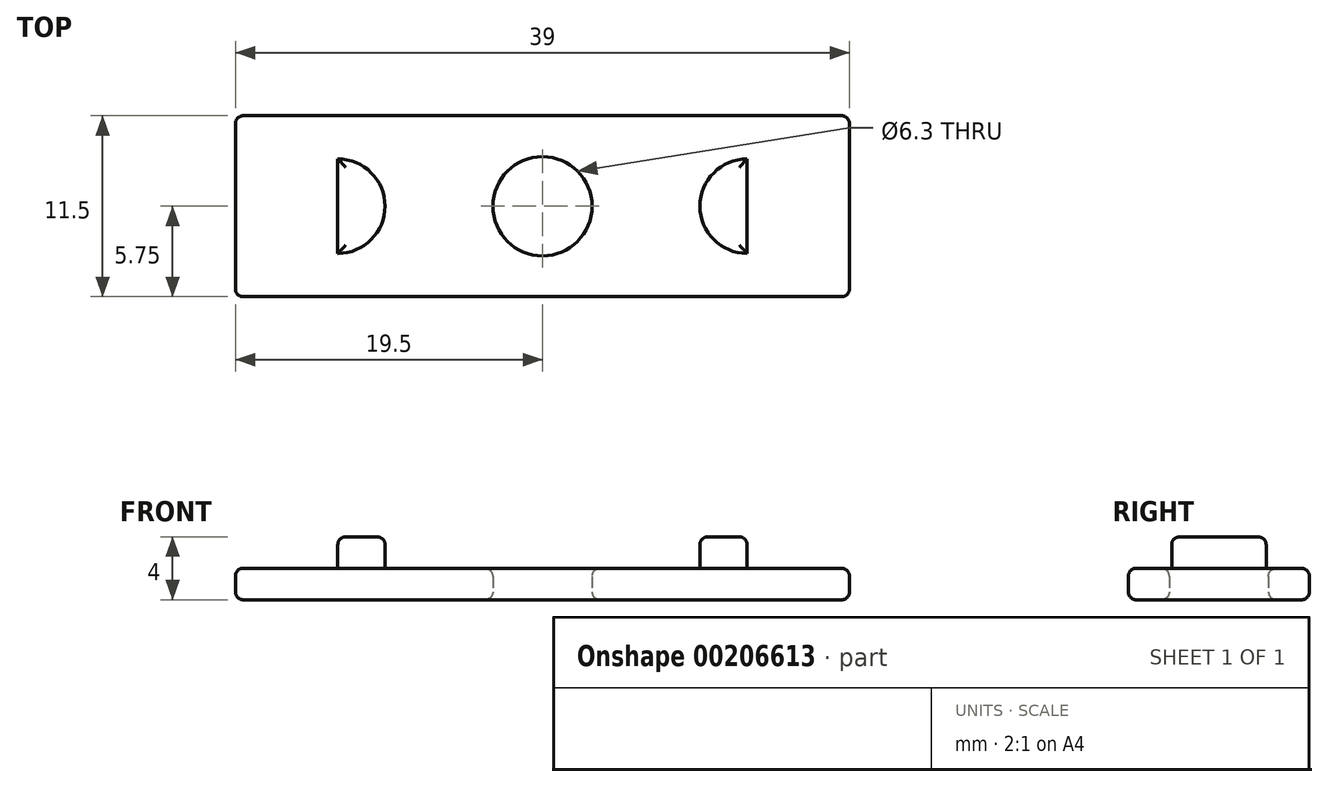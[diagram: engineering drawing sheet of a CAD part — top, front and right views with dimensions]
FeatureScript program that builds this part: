
annotation { "Feature Type Name" : "Feature", "Feature Type Description" : "" }
export const myFeature = defineFeature(function(context is Context, id is Id, definition is map)
    precondition{}
    {
        {
            var Q0;
            Q0=qCreatedBy(makeId("Top.planeOp"),FACE);
            var sketch = newSketch(context, id + "F0", { "sketchPlane" : qUnion([Q0])});
            skLineSegment(sketch, "E0.bottom", {"start": v(-19.5, 5.75) * mm, "end": v(19.5, 5.75) * mm});
            skLineSegment(sketch, "E0.top", {"start": v(-19.5, -5.75) * mm, "end": v(19.5, -5.75) * mm});
            skLineSegment(sketch, "E0.left", {"start": v(-19.5, 5.75) * mm, "end": v(-19.5, -5.75) * mm});
            skLineSegment(sketch, "E0.right", {"start": v(19.5, 5.75) * mm, "end": v(19.5, -5.75) * mm});
            skCircle(sketch, "E1", {"center": v(0, 0) * mm, "radius": 3.15 * mm});
            skSolve(sketch);
        }
        {
            var Q0;
            Q0 = qSketchRegion(id + "F0", true);
            extrude(context, id + "F1", {"entities" : qUnion([Q0]), "depth" : 2 * mm});
        }
        {
            var Q0;
            Q0=makeQuery(id+"F1.opExtrude","CAP_FACE",FACE,{"disambiguationData":[OSD([sQuery(id+"F0.wireOp",EDGE,"E0.bottom"),sQuery(id+"F0.wireOp",EDGE,"E0.top"),sQuery(id+"F0.wireOp",EDGE,"E0.left"),sQuery(id+"F0.wireOp",EDGE,"E0.right"),sQuery(id+"F0.wireOp",EDGE,"E1")])],"isStart":false});
            var sketch = newSketch(context, id + "F2", { "sketchPlane" : qUnion([Q0])});
            skArc(sketch, "E2", {"start": v(-13, -3) * mm, "mid": v(-10, 0) * mm, "end": v(-13, 3) * mm});
            skArc(sketch, "E3.MirrorC", {"start": v(13, -3) * mm, "mid": v(10, 0) * mm, "end": v(13, 3) * mm});
            skLineSegment(sketch, "E4", {"start": v(-13, 3) * mm, "end": v(-13, -3) * mm});
            skLineSegment(sketch, "E5.MirrorCS", {"start": v(13, 3) * mm, "end": v(13, -3) * mm});
            skSolve(sketch);
        }
        {
            var Q0;
            Q0 = qSketchRegion(id + "F2", true);
            extrude(context, id + "F3", {"entities" : qUnion([Q0]), "depth" : 2 * mm});
        }
        {
            var Q0;
            Q0=makeQuery(id+"F1.opExtrude","CAP_EDGE",EDGE,{"disambiguationData":[OSD([sQuery(id+"F0.wireOp",EDGE,"E1")])],"isStart":false});
            var Q1;
            Q1=makeQuery(id+"F1.opExtrude","CAP_EDGE",EDGE,{"disambiguationData":[OSD([sQuery(id+"F0.wireOp",EDGE,"E0.left")])],"isStart":true});
            var Q2;
            Q2=makeQuery(id+"F1.opExtrude","CAP_EDGE",EDGE,{"disambiguationData":[OSD([sQuery(id+"F0.wireOp",EDGE,"E0.right")])],"isStart":true});
            var Q3;
            Q3=makeQuery(id+"F1.opExtrude","CAP_EDGE",EDGE,{"disambiguationData":[OSD([sQuery(id+"F0.wireOp",EDGE,"E0.bottom")])],"isStart":true});
            var Q4;
            Q4=makeQuery(id+"F1.opExtrude","SWEPT_EDGE",EDGE,{"disambiguationData":[OSD([sQuery(id+"F0.wireOp",EDGE,"E0.bottom"),sQuery(id+"F0.wireOp",EDGE,"E0.right")])]});
            var Q5;
            Q5=makeQuery(id+"F1.opExtrude","SWEPT_EDGE",EDGE,{"disambiguationData":[OSD([sQuery(id+"F0.wireOp",EDGE,"E0.top"),sQuery(id+"F0.wireOp",EDGE,"E0.right")])]});
            var Q6;
            Q6=makeQuery(id+"F1.opExtrude","CAP_EDGE",EDGE,{"disambiguationData":[OSD([sQuery(id+"F0.wireOp",EDGE,"E0.bottom")])],"isStart":false});
            var Q7;
            Q7=makeQuery(id+"F1.opExtrude","SWEPT_EDGE",EDGE,{"disambiguationData":[OSD([sQuery(id+"F0.wireOp",EDGE,"E0.bottom"),sQuery(id+"F0.wireOp",EDGE,"E0.left")])]});
            var Q8;
            Q8=makeQuery(id+"F1.opExtrude","CAP_EDGE",EDGE,{"disambiguationData":[OSD([sQuery(id+"F0.wireOp",EDGE,"E0.left")])],"isStart":false});
            var Q9;
            Q9=makeQuery(id+"F1.opExtrude","SWEPT_EDGE",EDGE,{"disambiguationData":[OSD([sQuery(id+"F0.wireOp",EDGE,"E0.top"),sQuery(id+"F0.wireOp",EDGE,"E0.left")])]});
            var Q10;
            Q10=makeQuery(id+"F1.opExtrude","CAP_EDGE",EDGE,{"disambiguationData":[OSD([sQuery(id+"F0.wireOp",EDGE,"E0.top")])],"isStart":false});
            var Q11;
            Q11=makeQuery(id+"F1.opExtrude","CAP_FACE",FACE,{"disambiguationData":[OSD([sQuery(id+"F0.wireOp",EDGE,"E0.bottom"),sQuery(id+"F0.wireOp",EDGE,"E0.top"),sQuery(id+"F0.wireOp",EDGE,"E0.left"),sQuery(id+"F0.wireOp",EDGE,"E0.right"),sQuery(id+"F0.wireOp",EDGE,"E1")])],"isStart":false});
            var Q12;
            Q12=makeQuery(id+"F1.opExtrude","CAP_EDGE",EDGE,{"disambiguationData":[OSD([sQuery(id+"F0.wireOp",EDGE,"E0.top")])],"isStart":true});
            var Q13;
            Q13=makeQuery(id+"F1.opExtrude","CAP_EDGE",EDGE,{"disambiguationData":[OSD([sQuery(id+"F0.wireOp",EDGE,"E1")])],"isStart":true});
            var Q14;
            Q14=makeQuery(id+"F3.opExtrude","CAP_EDGE",EDGE,{"disambiguationData":[OSD([sQuery(id+"F2.wireOp",EDGE,"E3.MirrorC")])],"isStart":false});
            var Q15;
            Q15=makeQuery(id+"F3.opExtrude","CAP_EDGE",EDGE,{"disambiguationData":[OSD([sQuery(id+"F2.wireOp",EDGE,"E2")])],"isStart":false});
            var Q16;
            Q16=makeQuery(id+"F3.opExtrude","CAP_EDGE",EDGE,{"disambiguationData":[OSD([sQuery(id+"F2.wireOp",EDGE,"E4")])],"isStart":false});
            var Q17;
            Q17=makeQuery(id+"F3.opExtrude","CAP_EDGE",EDGE,{"disambiguationData":[OSD([sQuery(id+"F2.wireOp",EDGE,"E5.MirrorCS")])],"isStart":false});
            fillet(context, id + "F4", {"entities" : qUnion([Q0, Q1, Q2, Q3, Q4, Q5, Q6, Q7, Q8, Q9, Q10, Q11, Q12, Q13, Q14, Q15, Q16, Q17]), "radius" : .5 * mm, "tangentPropagation" : true, "allowEdgeOverflow" : false});
        }
    });
